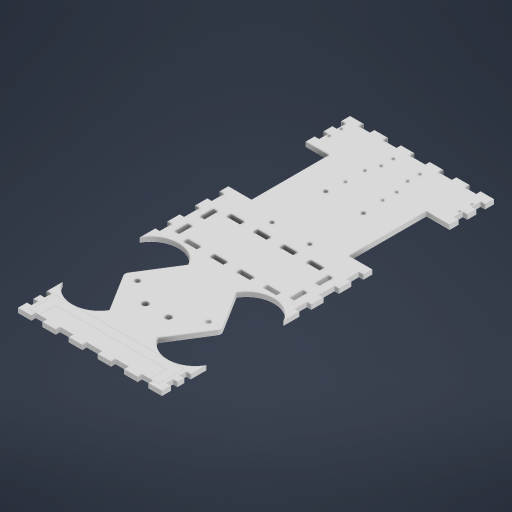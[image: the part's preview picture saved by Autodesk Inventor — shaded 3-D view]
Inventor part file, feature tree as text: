
AUTODESK INVENTOR PART (.ipt)
format: ipt  version: 2023.2 (Build 272271000, 271)  size: 606,720 bytes
history: native  units: mm
features: sketch x7, hole x5, other x1
ambient origin geometry x8: Origin, YZ Plane, XZ Plane, XY Plane, X Axis, Y Axis, Z Axis, Center Point
bodies: Body1 (feature_tree)
feature tree (13):
  hole  "Hole1"  [1 undecoded]
  hole  "Hole2"  [1 undecoded]
  hole  "Hole3"  [1 undecoded]
  other  "Mark1"
  hole  "Hole4"  [1 undecoded]
  hole  "Hole5"  [1 undecoded]
  sketch  "Sketch1"  dims[d122=130.0mm d123=300.0mm]
  sketch  "Sketch3"  dims[d128=75.0mm d158=33.0mm]
  sketch  "Sketch4"  dims[d159=6.108652mm d160=6.108652mm]
  sketch  "Sketch5"  dims[d161=4.0mm d169=6.108652mm d170=6.108652mm d172=75.0mm]
  sketch  "Sketch7"  dims[d175=33.0mm d179=33.0mm]
  sketch  "Sketch8"  dims[d181=4.0mm d182=0.0mm]
  sketch  "Sketch9"  dims[d183=70.0mm d186=35.0mm d187=21.0mm d188=75.0mm d189=70.0mm d190=21.0mm d191=75.0mm d196=3.0mm d201=34.0mm d202=48.5mm d205=75.0mm d208=3.0mm d209=5.0mm d210=3.0mm d211=6.0mm d212=4.0mm d213=2.0mm d214=90.0deg d215=8.0mm d216=20.594885mm d217=75.0mm d219=4.0mm d220=33.0mm d221=4.0mm d222=6.0mm d223=4.0mm d224=2.0mm d225=90.0deg d226=8.0mm d227=20.594885mm d228=21.0mm d229=5.0mm d231=21.0mm d233=14.5mm d234=5.0mm d235=6.0mm d236=4.0mm d237=2.0mm d238=90.0deg d239=8.0mm d240=20.594885mm d242=6.0mm d244=4.0mm d245=6.0mm d246=6.0mm d252=11.0mm d253=14.0mm d256=14.0mm d257=11.0mm d259=11.0mm d263=11.0mm d264=8.0mm d265=8.0mm d266=8.0mm d267=8.0mm d268=8.0mm d269=8.0mm d270=4.0mm d271=0.0mm d272=12.0mm d273=10.0mm d274=12.0mm d275=14.0mm d276=12.0mm d277=10.0mm d278=12.0mm d279=12.0mm d280=12.0mm d281=12.0mm d282=12.0mm d284=10.0mm d285=12.0mm d286=14.0mm d287=12.0mm d288=10.0mm d294=12.0mm d295=12.0mm d296=12.0mm d297=12.0mm d298=12.0mm d299=12.0mm d300=14.0mm d301=8.0mm d308=116.0mm d309=8.0mm d310=8.0mm d311=23.031521mm d313=35.0mm d316=12.0mm d318=12.0mm d319=100.0mm d320=4.0mm d321=12.0mm d323=8.0mm d324=12.0mm d326=16.0mm d327=4.0mm d328=0.0mm d329=2.0mm d330=15.0mm d333=2.0mm d334=11.0mm d339=47.0mm d341=2.0mm d342=17.65mm d346=2.5mm d347=2.5mm d348=31.2mm d349=32.0mm d352=2.0mm d353=6.0mm d354=4.0mm d355=2.0mm d356=90.0deg d357=8.0mm d358=20.594885mm d359=2.0mm d360=6.0mm d361=4.0mm d362=2.0mm d363=90.0deg d364=8.0mm d365=20.594885mm d9=0.5mm d10=0.872665mm d11=0.5mm d12=0.872665mm d13=0.5mm d14=0.872665mm d27=0.5mm d28=0.872665mm d29=0.5mm d30=0.872665mm d88=0.5mm d89=0.872665mm d90=0.5mm d91=0.872665mm d116=0.5mm d117=0.872665mm d118=0.5mm d119=0.872665mm d154=0.5mm d155=0.872665mm d156=0.5mm d157=0.872665mm d184=0.872665mm]
note: 5 required parameter values undecoded (feature->parameter linkage not recoverable at this tier; creation-order binding heuristic only, values carry confidence <= 0.55)
